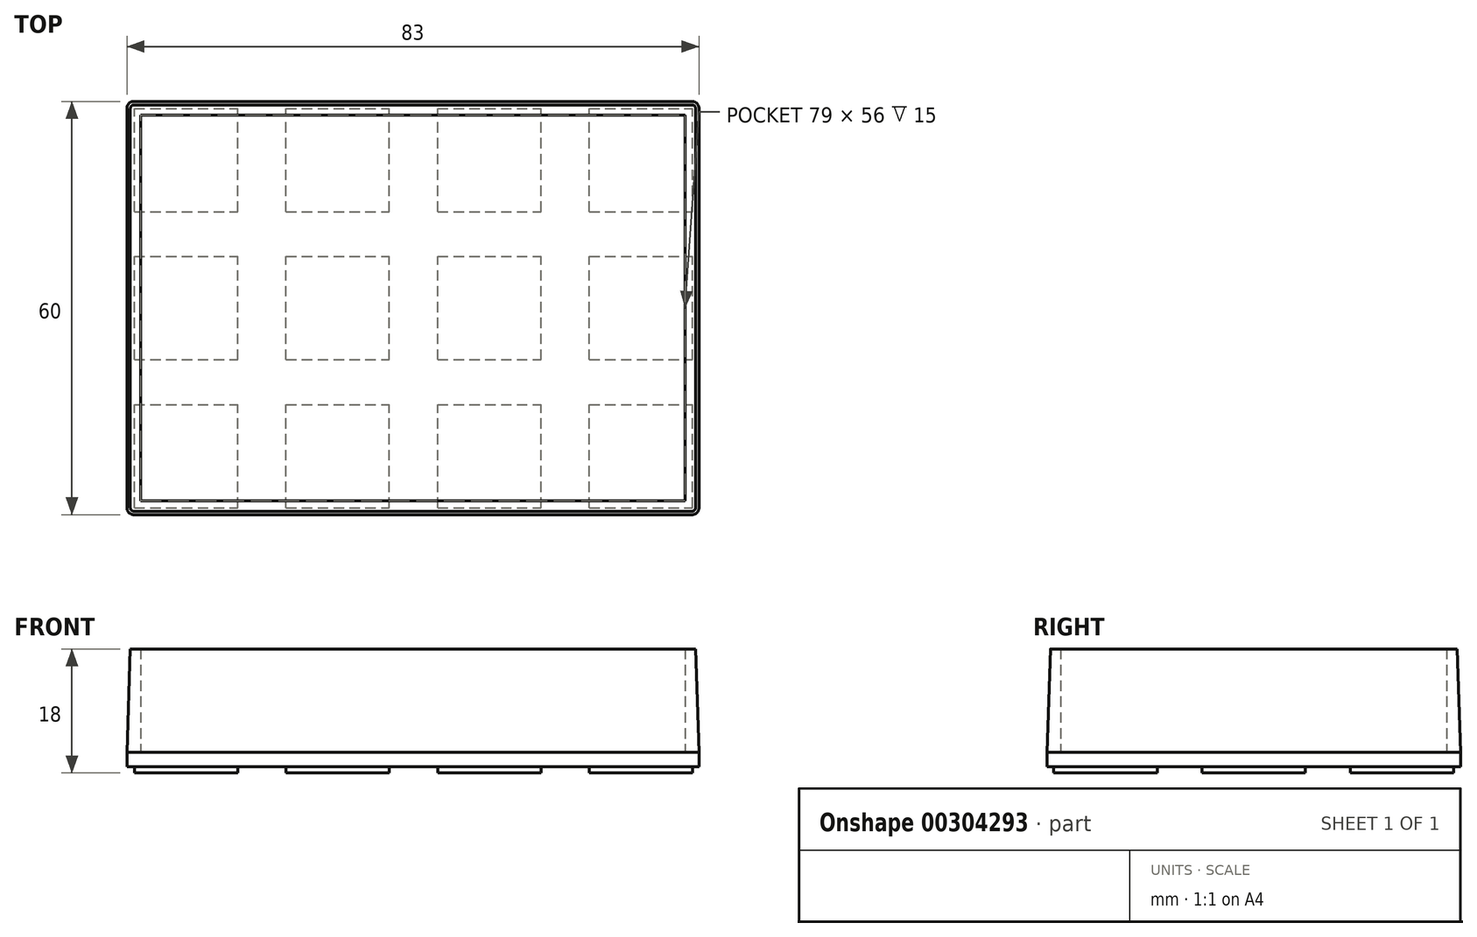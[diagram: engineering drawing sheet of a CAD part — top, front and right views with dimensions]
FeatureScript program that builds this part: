
annotation { "Feature Type Name" : "Feature", "Feature Type Description" : "" }
export const myFeature = defineFeature(function(context is Context, id is Id, definition is map)
    precondition{}
    {
        {
            var Q0;
            Q0=qCreatedBy(makeId("Top.planeOp"),FACE);
            var sketch = newSketch(context, id + "F0", { "sketchPlane" : qUnion([Q0])});
            skLineSegment(sketch, "E0.bottom", {"start": v(-38.66, 16.7) * mm, "end": v(42.34, 16.7) * mm});
            skLineSegment(sketch, "E0.top", {"start": v(-38.66, -43.3) * mm, "end": v(42.34, -43.3) * mm});
            skLineSegment(sketch, "E0.left", {"start": v(-39.66, 15.7) * mm, "end": v(-39.66, -42.3) * mm});
            skLineSegment(sketch, "E0.right", {"start": v(43.34, 15.7) * mm, "end": v(43.34, -42.3) * mm});
            skLineSegment(sketch, "E1.0", {"start": v(-37.66, 14.7) * mm, "end": v(41.34, 14.7) * mm});
            skLineSegment(sketch, "E2.0", {"start": v(-37.66, 14.7) * mm, "end": v(-37.66, -41.3) * mm});
            skLineSegment(sketch, "E3.0", {"start": v(-37.66, -41.3) * mm, "end": v(41.34, -41.3) * mm});
            skLineSegment(sketch, "E4.0", {"start": v(41.34, 14.7) * mm, "end": v(41.34, -41.3) * mm});
            skPoint(sketch, "E5.visualSharp", {"position": v(-39.66, 16.7) * mm});
            skArc(sketch, "E5.filletArc", {"start": v(-38.66, 16.7) * mm, "mid": v(-39.37, 16.42) * mm, "end": v(-39.66, 15.7) * mm});
            skPoint(sketch, "E6.visualSharp", {"position": v(43.34, 16.7) * mm});
            skArc(sketch, "E6.filletArc", {"start": v(43.34, 15.7) * mm, "mid": v(43.04, 16.42) * mm, "end": v(42.34, 16.7) * mm});
            skPoint(sketch, "E7.visualSharp", {"position": v(43.34, -43.3) * mm});
            skArc(sketch, "E7.filletArc", {"start": v(42.34, -43.3) * mm, "mid": v(43.04, -43) * mm, "end": v(43.34, -42.3) * mm});
            skPoint(sketch, "E8.visualSharp", {"position": v(-39.66, -43.3) * mm});
            skArc(sketch, "E8.filletArc", {"start": v(-39.66, -42.3) * mm, "mid": v(-39.37, -43) * mm, "end": v(-38.66, -43.3) * mm});
            skSolve(sketch);
        }
        {
            var Q0;
            Q0=qCreatedBy(makeId("Top.planeOp"),FACE);
            cPlane(context, id + "F1", {"entities" : qUnion([Q0]), "cplaneType" : CPlaneType.OFFSET, "offset" : 2 * mm, "oppositeDirection" : true, "width" : 150 * mm, "height" : 150 * mm});
        }
        {
            var Q0;
            Q0=qCreatedBy(id+"F1.planeOp",FACE);
            var sketch = newSketch(context, id + "F2", { "sketchPlane" : qUnion([Q0])});
            skLineSegment(sketch, "E9.bottom", {"start": v(-38.58, -42.3) * mm, "end": v(-23.58, -42.3) * mm});
            skLineSegment(sketch, "E9.top", {"start": v(-38.58, -27.3) * mm, "end": v(-23.58, -27.3) * mm});
            skLineSegment(sketch, "E9.left", {"start": v(-38.58, -42.3) * mm, "end": v(-38.58, -27.3) * mm});
            skLineSegment(sketch, "E9.right", {"start": v(-23.58, -42.3) * mm, "end": v(-23.58, -27.3) * mm});
            skLineSegment(sketch, "E10.0.1.0", {"start": v(-23.58, -20.8) * mm, "end": v(-23.58, -5.8) * mm});
            skLineSegment(sketch, "E10.0.1.1", {"start": v(-38.58, -20.8) * mm, "end": v(-23.58, -20.8) * mm});
            skLineSegment(sketch, "E10.0.1.2", {"start": v(-38.58, -20.8) * mm, "end": v(-38.58, -5.8) * mm});
            skLineSegment(sketch, "E10.0.1.3", {"start": v(-38.58, -5.8) * mm, "end": v(-23.58, -5.8) * mm});
            skLineSegment(sketch, "E10.0.2.0", {"start": v(-23.58, 0.7) * mm, "end": v(-23.58, 15.7) * mm});
            skLineSegment(sketch, "E10.0.2.1", {"start": v(-38.58, 0.7) * mm, "end": v(-23.58, 0.7) * mm});
            skLineSegment(sketch, "E10.0.2.2", {"start": v(-38.58, 0.7) * mm, "end": v(-38.58, 15.7) * mm});
            skLineSegment(sketch, "E10.0.2.3", {"start": v(-38.58, 15.7) * mm, "end": v(-23.58, 15.7) * mm});
            skLineSegment(sketch, "E10.1.0.0", {"start": v(-1.58, -42.3) * mm, "end": v(-1.58, -27.3) * mm});
            skLineSegment(sketch, "E10.1.0.1", {"start": v(-16.58, -42.3) * mm, "end": v(-1.58, -42.3) * mm});
            skLineSegment(sketch, "E10.1.0.2", {"start": v(-16.58, -42.3) * mm, "end": v(-16.58, -27.3) * mm});
            skLineSegment(sketch, "E10.1.0.3", {"start": v(-16.58, -27.3) * mm, "end": v(-1.58, -27.3) * mm});
            skLineSegment(sketch, "E10.1.1.0", {"start": v(-1.58, -20.8) * mm, "end": v(-1.58, -5.8) * mm});
            skLineSegment(sketch, "E10.1.1.1", {"start": v(-16.58, -20.8) * mm, "end": v(-1.58, -20.8) * mm});
            skLineSegment(sketch, "E10.1.1.2", {"start": v(-16.58, -20.8) * mm, "end": v(-16.58, -5.8) * mm});
            skLineSegment(sketch, "E10.1.1.3", {"start": v(-16.58, -5.8) * mm, "end": v(-1.58, -5.8) * mm});
            skLineSegment(sketch, "E10.1.2.0", {"start": v(-1.58, 0.7) * mm, "end": v(-1.58, 15.7) * mm});
            skLineSegment(sketch, "E10.1.2.1", {"start": v(-16.58, 0.7) * mm, "end": v(-1.58, 0.7) * mm});
            skLineSegment(sketch, "E10.1.2.2", {"start": v(-16.58, 0.7) * mm, "end": v(-16.58, 15.7) * mm});
            skLineSegment(sketch, "E10.1.2.3", {"start": v(-16.58, 15.7) * mm, "end": v(-1.58, 15.7) * mm});
            skLineSegment(sketch, "E10.2.0.0", {"start": v(20.42, -42.3) * mm, "end": v(20.42, -27.3) * mm});
            skLineSegment(sketch, "E10.2.0.1", {"start": v(5.42, -42.3) * mm, "end": v(20.42, -42.3) * mm});
            skLineSegment(sketch, "E10.2.0.2", {"start": v(5.42, -42.3) * mm, "end": v(5.42, -27.3) * mm});
            skLineSegment(sketch, "E10.2.0.3", {"start": v(5.42, -27.3) * mm, "end": v(20.42, -27.3) * mm});
            skLineSegment(sketch, "E10.2.1.0", {"start": v(20.42, -20.8) * mm, "end": v(20.42, -5.8) * mm});
            skLineSegment(sketch, "E10.2.1.1", {"start": v(5.42, -20.8) * mm, "end": v(20.42, -20.8) * mm});
            skLineSegment(sketch, "E10.2.1.2", {"start": v(5.42, -20.8) * mm, "end": v(5.42, -5.8) * mm});
            skLineSegment(sketch, "E10.2.1.3", {"start": v(5.42, -5.8) * mm, "end": v(20.42, -5.8) * mm});
            skLineSegment(sketch, "E10.2.2.0", {"start": v(20.42, 0.7) * mm, "end": v(20.42, 15.7) * mm});
            skLineSegment(sketch, "E10.2.2.1", {"start": v(5.42, 0.7) * mm, "end": v(20.42, 0.7) * mm});
            skLineSegment(sketch, "E10.2.2.2", {"start": v(5.42, 0.7) * mm, "end": v(5.42, 15.7) * mm});
            skLineSegment(sketch, "E10.2.2.3", {"start": v(5.42, 15.7) * mm, "end": v(20.42, 15.7) * mm});
            skLineSegment(sketch, "E10.3.0.0", {"start": v(42.42, -42.3) * mm, "end": v(42.42, -27.3) * mm});
            skLineSegment(sketch, "E10.3.0.1", {"start": v(27.42, -42.3) * mm, "end": v(42.42, -42.3) * mm});
            skLineSegment(sketch, "E10.3.0.2", {"start": v(27.42, -42.3) * mm, "end": v(27.42, -27.3) * mm});
            skLineSegment(sketch, "E10.3.0.3", {"start": v(27.42, -27.3) * mm, "end": v(42.42, -27.3) * mm});
            skLineSegment(sketch, "E10.3.1.0", {"start": v(42.42, -20.8) * mm, "end": v(42.42, -5.8) * mm});
            skLineSegment(sketch, "E10.3.1.1", {"start": v(27.42, -20.8) * mm, "end": v(42.42, -20.8) * mm});
            skLineSegment(sketch, "E10.3.1.2", {"start": v(27.42, -20.8) * mm, "end": v(27.42, -5.8) * mm});
            skLineSegment(sketch, "E10.3.1.3", {"start": v(27.42, -5.8) * mm, "end": v(42.42, -5.8) * mm});
            skLineSegment(sketch, "E10.3.2.0", {"start": v(42.42, 0.7) * mm, "end": v(42.42, 15.7) * mm});
            skLineSegment(sketch, "E10.3.2.1", {"start": v(27.42, 0.7) * mm, "end": v(42.42, 0.7) * mm});
            skLineSegment(sketch, "E10.3.2.2", {"start": v(27.42, 0.7) * mm, "end": v(27.42, 15.7) * mm});
            skLineSegment(sketch, "E10.3.2.3", {"start": v(27.42, 15.7) * mm, "end": v(42.42, 15.7) * mm});
            skLineSegment(sketch, "E10.direction1", {"start": v(-38.58, -42.3) * mm, "end": v(-16.58, -42.3) * mm, "construction": true});
            skLineSegment(sketch, "E10.direction2", {"start": v(-38.58, -42.3) * mm, "end": v(-38.58, -20.8) * mm, "construction": true});
            skSolve(sketch);
        }
        {
            var Q0;
            Q0 = qSketchRegion(id + "F2", true);
            extrude(context, id + "F3", {"entities" : qUnion([Q0]), "oppositeDirection" : true, "depth" : 1 * mm});
        }
        {
            var Q0;
            Q0 = qSketchRegion(id + "F0", true);
            var Q1;
            Q1=makeQuery(id+"F0.imprint","IMPRINT",FACE,{"disambiguationData":[TD([[makeQuery(id+"F0.imprint","IMPRINT",EDGE,{"derivedFrom":sQuery(id+"F0.wireOp",EDGE,"E1.0")}),-1.0]])]});
            extrude(context, id + "F4", {"entities" : qUnion([Q0, Q1]), "oppositeDirection" : true, "depth" : 2.1 * mm});
        }
        {
            var Q0;
            Q0 = qSketchRegion(id + "F0", true);
            extrude(context, id + "F5", {"entities" : qUnion([Q0]), "operationType" : NewBodyOperationType.ADD, "depth" : 15 * mm});
        }
        {
            var Q0;
            Q0=makeQuery(id+"F5.opExtrude","CAP_EDGE",EDGE,{"disambiguationData":[OSD([sQuery(id+"F0.wireOp",EDGE,"E0.right")])],"isStart":false});
            chamfer(context, id + "F6", {"entities" : qUnion([Q0]), "chamferType" : ChamferType.TWO_OFFSETS, "width1" : 0.5 * mm, "oppositeDirection" : true, "width2" : 15 * mm, "tangentPropagation" : true});
        }
    });
